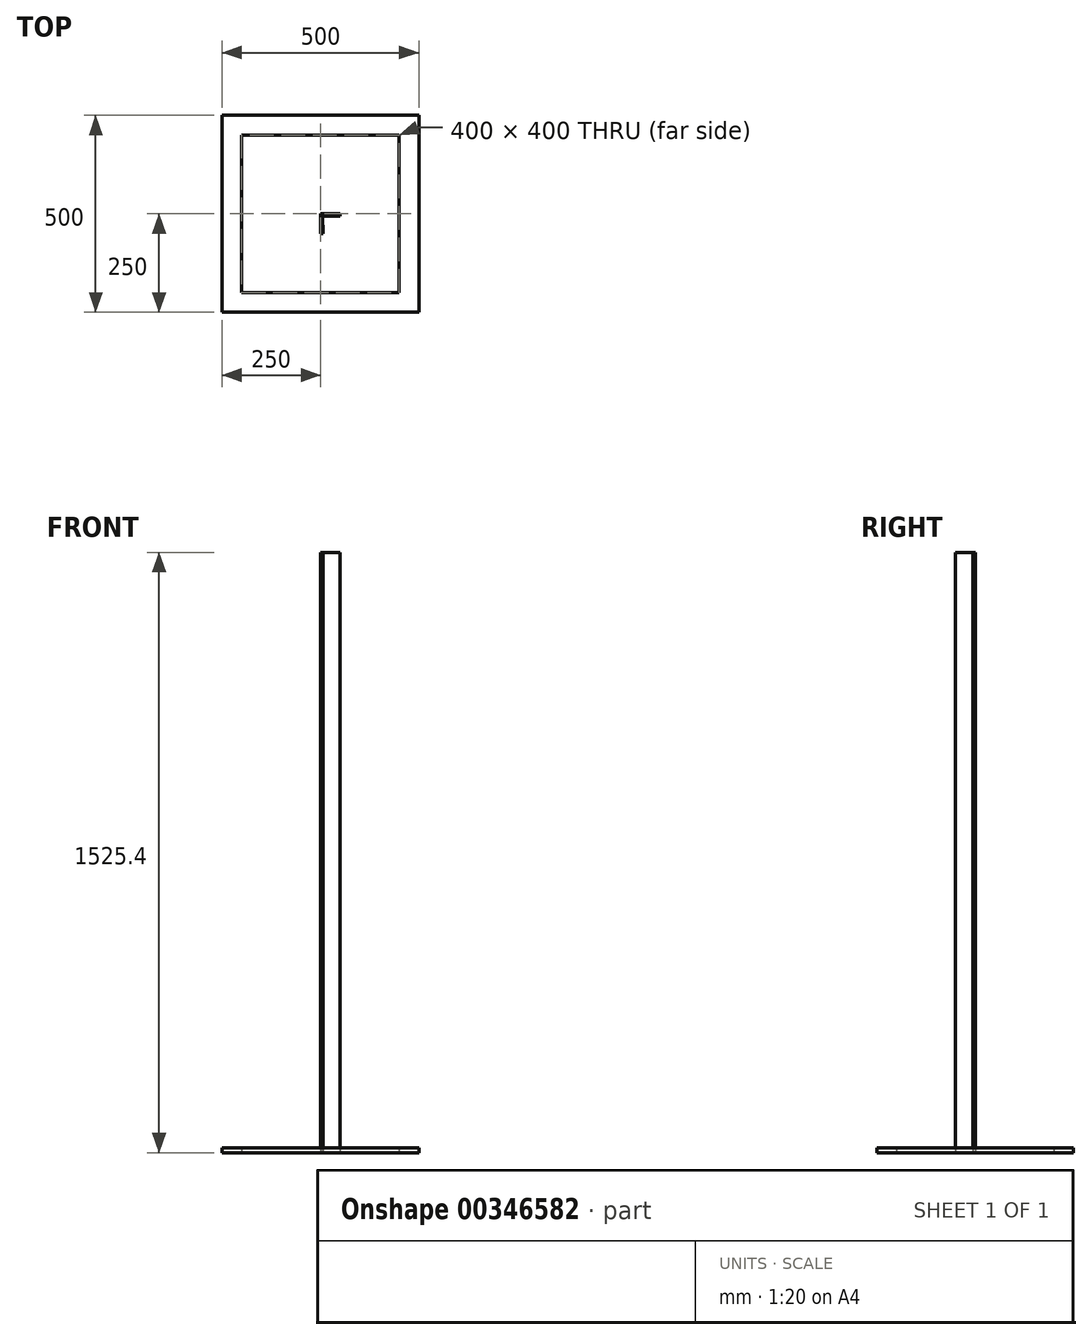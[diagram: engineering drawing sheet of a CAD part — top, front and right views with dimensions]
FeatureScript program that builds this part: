
annotation { "Feature Type Name" : "Feature", "Feature Type Description" : "" }
export const myFeature = defineFeature(function(context is Context, id is Id, definition is map)
    precondition{}
    {
        {
            var Q0;
            Q0=qCreatedBy(makeId("Top.planeOp"),FACE);
            var sketch = newSketch(context, id + "F0", { "sketchPlane" : qUnion([Q0])});
            skLineSegment(sketch, "E0", {"start": v(0, 0) * mm, "end": v(50, 0) * mm});
            skLineSegment(sketch, "E1", {"start": v(50, 0) * mm, "end": v(50, -6) * mm});
            skLineSegment(sketch, "E2", {"start": v(50, -6) * mm, "end": v(5.7, -6) * mm});
            skLineSegment(sketch, "E3", {"start": v(5.7, -6) * mm, "end": v(6, -49.96) * mm});
            skLineSegment(sketch, "E4", {"start": v(6, -49.96) * mm, "end": v(0, -50) * mm});
            skLineSegment(sketch, "E5", {"start": v(0, -50) * mm, "end": v(0, 0) * mm});
            skSolve(sketch);
        }
        {
            var Q0;
            Q0=makeQuery(id+"F0.imprint","IMPRINT",FACE,{"disambiguationData":[TD([[makeQuery(id+"F0.imprint","IMPRINT",EDGE,{"derivedFrom":sQuery(id+"F0.wireOp",EDGE,"E0")}),-1.0]])]});
            extrude(context, id + "F1", {"entities" : qUnion([Q0]), "depth" : 1525.4 * mm});
        }
        {
            var Q0;
            Q0=qCreatedBy(makeId("Top.planeOp"),FACE);
            var sketch = newSketch(context, id + "F2", { "sketchPlane" : qUnion([Q0])});
            skLineSegment(sketch, "E6.bottom", {"start": v(250, -250) * mm, "end": v(-250, -250) * mm});
            skLineSegment(sketch, "E6.top", {"start": v(250, 250) * mm, "end": v(-250, 250) * mm});
            skLineSegment(sketch, "E6.left", {"start": v(250, -250) * mm, "end": v(250, 250) * mm});
            skLineSegment(sketch, "E6.right", {"start": v(-250, -250) * mm, "end": v(-250, 250) * mm});
            skPoint(sketch, "E6.middle", {"position": v(0, 0) * mm});
            skLineSegment(sketch, "E7.bottom", {"start": v(200, -200) * mm, "end": v(-200, -200) * mm});
            skLineSegment(sketch, "E7.top", {"start": v(200, 200) * mm, "end": v(-200, 200) * mm});
            skLineSegment(sketch, "E7.left", {"start": v(200, -200) * mm, "end": v(200, 200) * mm});
            skLineSegment(sketch, "E7.right", {"start": v(-200, -200) * mm, "end": v(-200, 200) * mm});
            skSolve(sketch);
        }
        {
            var Q0;
            Q0=makeQuery(id+"F2.imprint","IMPRINT",FACE,{"disambiguationData":[TD([[makeQuery(id+"F2.imprint","IMPRINT",EDGE,{"derivedFrom":sQuery(id+"F2.wireOp",EDGE,"E6.bottom")}),-1.0]])]});
            extrude(context, id + "F3", {"entities" : qUnion([Q0]), "depth" : 12 * mm});
        }
    });
